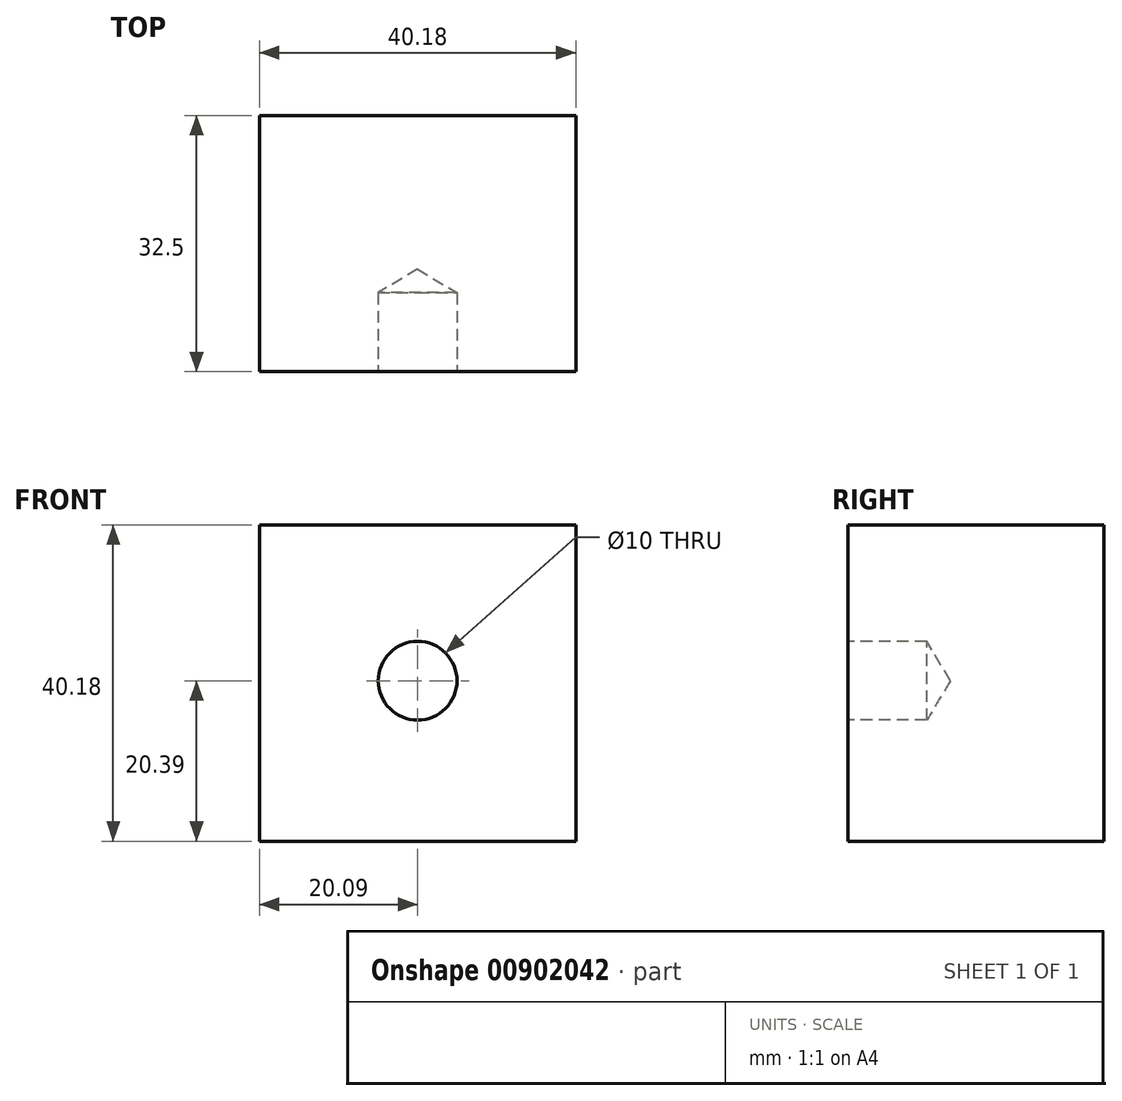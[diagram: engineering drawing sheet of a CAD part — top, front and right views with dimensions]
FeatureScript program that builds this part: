
annotation { "Feature Type Name" : "Feature", "Feature Type Description" : "" }
export const myFeature = defineFeature(function(context is Context, id is Id, definition is map)
    precondition{}
    {
        {
            var Q0;
            Q0=qCreatedBy(makeId("Front.planeOp"),FACE);
            var sketch = newSketch(context, id + "F0", { "sketchPlane" : qUnion([Q0])});
            skLineSegment(sketch, "E0", {"start": v(-55.06, 19.79) * mm, "end": v(-14.88, 19.79) * mm});
            skLineSegment(sketch, "E1", {"start": v(-14.88, 19.79) * mm, "end": v(-14.88, -20.4) * mm});
            skLineSegment(sketch, "E2", {"start": v(-14.88, -20.4) * mm, "end": v(-55.06, -20.4) * mm});
            skLineSegment(sketch, "E3", {"start": v(-55.06, -20.4) * mm, "end": v(-55.06, 19.79) * mm});
            skSolve(sketch);
        }
        {
            var Q0;
            Q0=makeQuery(id+"F0.imprint","IMPRINT",FACE,{"disambiguationData":[TD([[makeQuery(id+"F0.imprint","IMPRINT",EDGE,{"derivedFrom":sQuery(id+"F0.wireOp",EDGE,"E0")}),-1.0]])]});
            extrude(context, id + "F1", {"entities" : qUnion([Q0]), "depth" : 32.5 * mm, "offsetDistance" : 25 * mm});
        }
        {
            var Q0;
            Q0=makeQuery(id+"F1.opExtrude","CAP_FACE",FACE,{"disambiguationData":[OSD([sQuery(id+"F0.wireOp",EDGE,"E0"),sQuery(id+"F0.wireOp",EDGE,"E1"),sQuery(id+"F0.wireOp",EDGE,"E2"),sQuery(id+"F0.wireOp",EDGE,"E3")])],"isStart":false});
            var sketch = newSketch(context, id + "F2", { "sketchPlane" : qUnion([Q0])});
            skPoint(sketch, "E4", {"position": v(-34.97, 0) * mm});
            skSolve(sketch);
        }
        {
            var Q0;
            Q0=sQuery(id+"F2.wireOp",VERTEX,"E4");
            var Q1;
            Q1=makeQuery(id+"F1.opExtrude","SWEPT_BODY",BODY,{"disambiguationData":[OSD([sQuery(id+"F0.wireOp",EDGE,"E0"),sQuery(id+"F0.wireOp",EDGE,"E1"),sQuery(id+"F0.wireOp",EDGE,"E2"),sQuery(id+"F0.wireOp",EDGE,"E3")])]});
            hole(context, id + "F3", {"style" : HoleStyle.SIMPLE, "endStyle" : HoleEndStyle.BLIND, "holeDiameter" : 10 * mm, "majorDiameter" : 5 * mm, "holeDepth" : 10 * mm, "isTappedThrough" : true, "tappedDepth" : 12 * mm, "tapClearance" : 3, "startFromSketch" : true, "locations" : qUnion([Q0]), "scope" : qUnion([Q1])});
        }
    });
